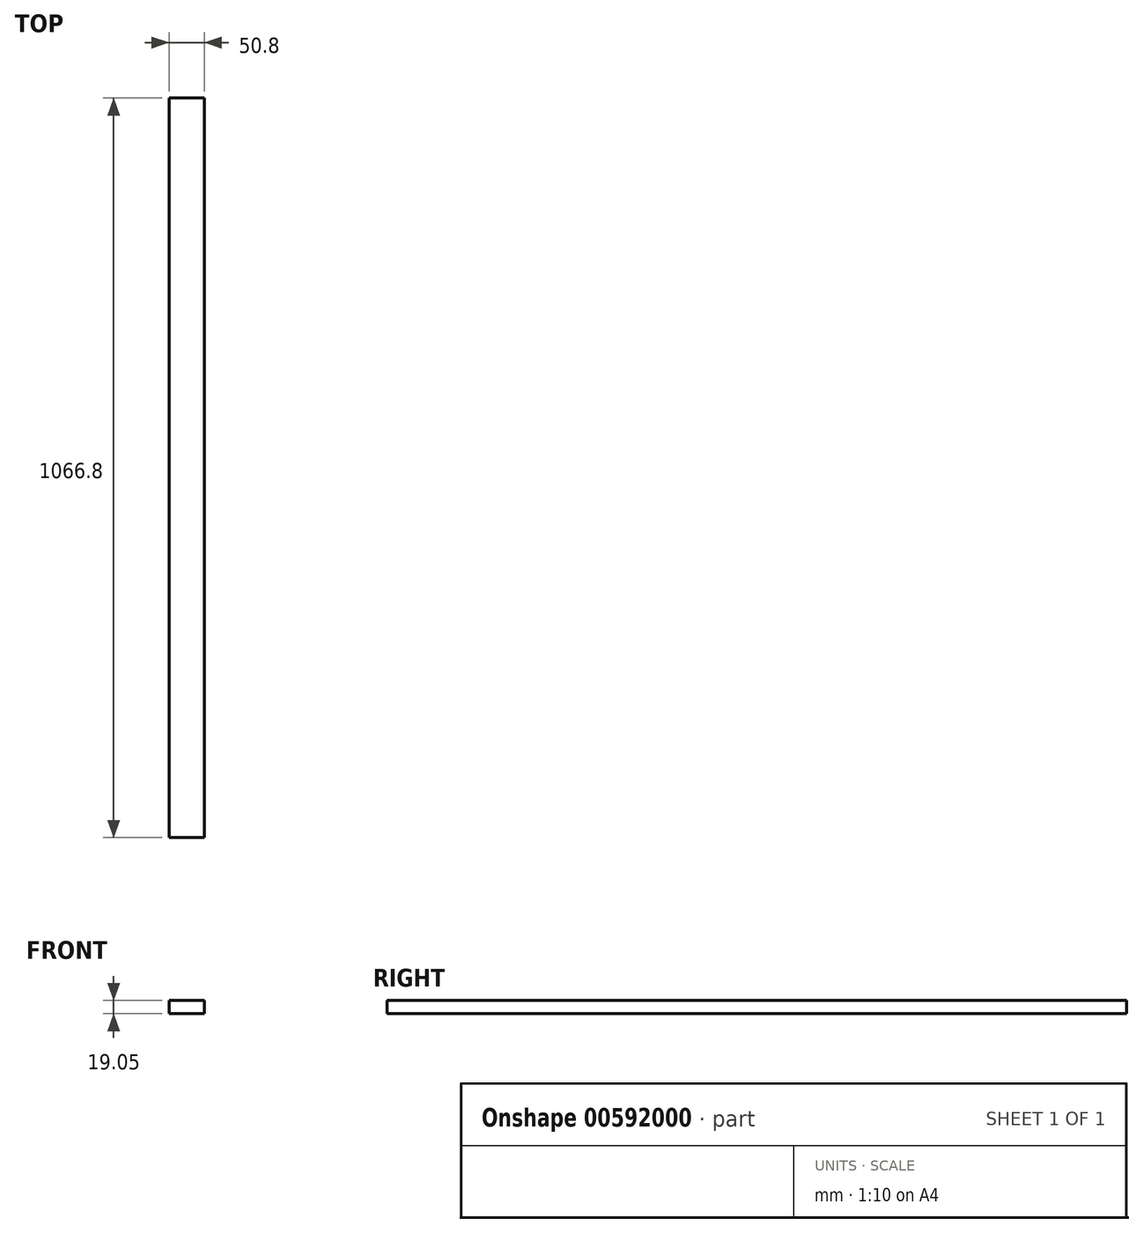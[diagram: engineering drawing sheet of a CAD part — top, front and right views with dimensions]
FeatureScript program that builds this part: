
annotation { "Feature Type Name" : "Feature", "Feature Type Description" : "" }
export const myFeature = defineFeature(function(context is Context, id is Id, definition is map)
    precondition{}
    {
        {
            var Q0;
            Q0=qCreatedBy(makeId("Top.planeOp"),FACE);
            var sketch = newSketch(context, id + "F0", { "sketchPlane" : qUnion([Q0])});
            skLineSegment(sketch, "E0.bottom", {"start": v(-52.93, 1019.8) * mm, "end": v(-2.13, 1019.8) * mm});
            skLineSegment(sketch, "E0.top", {"start": v(-52.93, -47) * mm, "end": v(-2.13, -47) * mm});
            skLineSegment(sketch, "E0.left", {"start": v(-52.93, 1019.8) * mm, "end": v(-52.93, -47) * mm});
            skLineSegment(sketch, "E0.right", {"start": v(-2.13, 1019.8) * mm, "end": v(-2.13, -47) * mm});
            skSolve(sketch);
        }
        {
            var Q0;
            Q0 = qSketchRegion(id + "F0", true);
            extrude(context, id + "F1", {"entities" : qUnion([Q0]), "depth" : 19.05 * mm, "offsetDistance" : 25.4 * mm});
        }
    });
